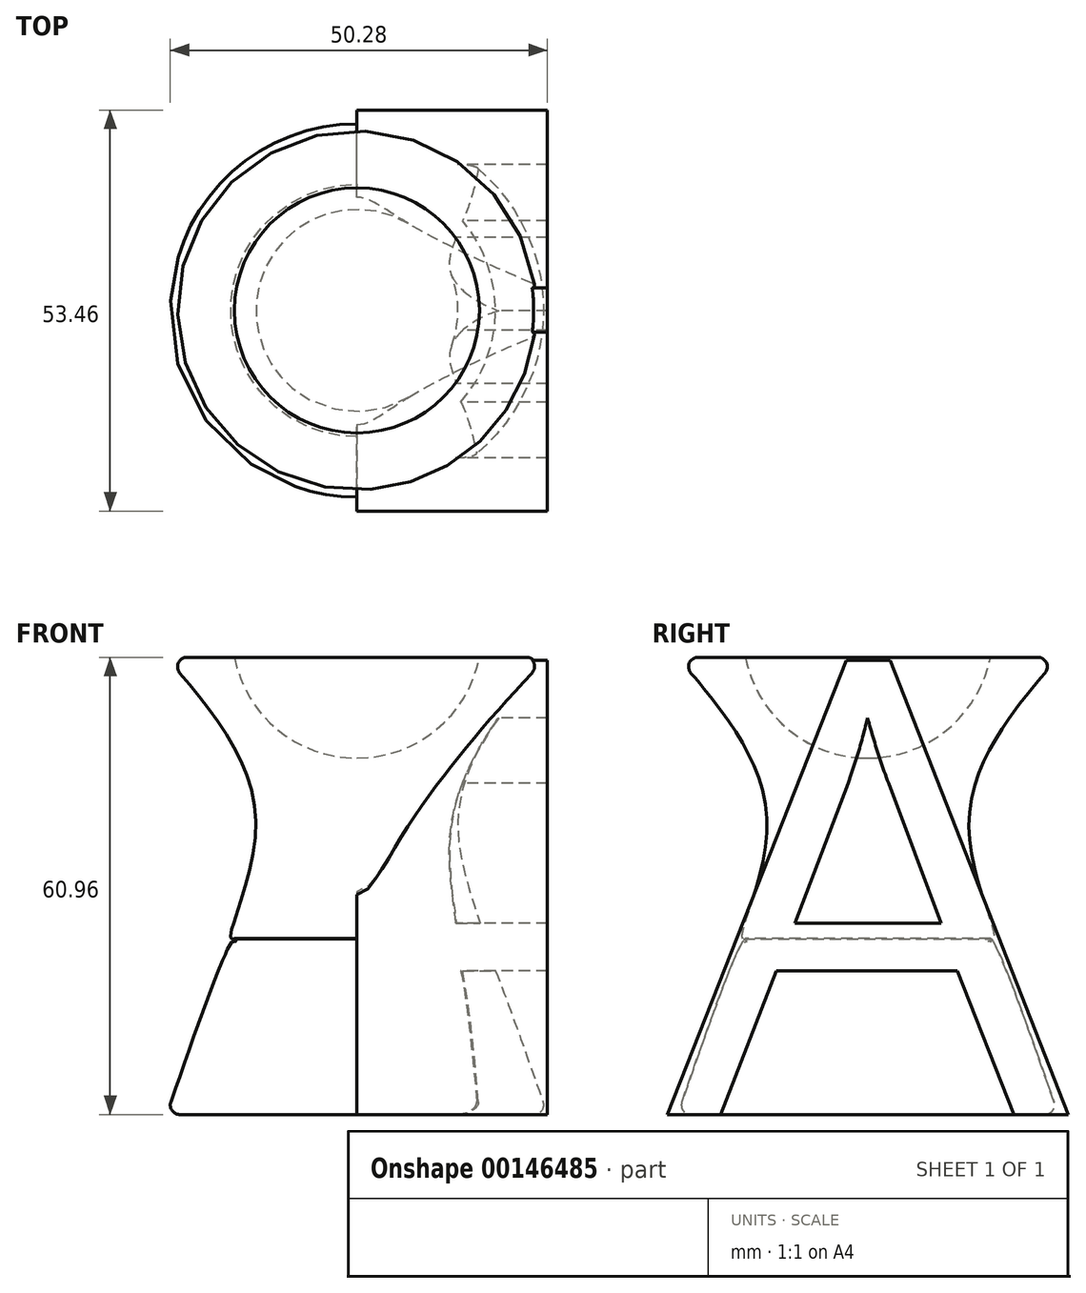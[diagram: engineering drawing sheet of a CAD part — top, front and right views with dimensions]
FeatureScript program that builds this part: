
annotation { "Feature Type Name" : "Feature", "Feature Type Description" : "" }
export const myFeature = defineFeature(function(context is Context, id is Id, definition is map)
    precondition{}
    {
        {
            var Q0;
            Q0=qCreatedBy(makeId("Top.planeOp"),FACE);
            var sketch = newSketch(context, id + "F0", { "sketchPlane" : qUnion([Q0])});
            skCircle(sketch, "E0", {"center": v(0, 0) * mm, "radius": 25.4 * mm});
            skSolve(sketch);
        }
        {
            var Q0;
            Q0=makeQuery(id+"F0.imprint","IMPRINT",FACE,{"disambiguationData":[TD([[makeQuery(id+"F0.imprint","IMPRINT",EDGE,{"derivedFrom":sQuery(id+"F0.wireOp",EDGE,"E0")}),1.0]])]});
            extrude(context, id + "F1", {"entities" : qUnion([Q0]), "depth" : 60.96 * mm});
        }
        {
            var Q0;
            Q0=qCreatedBy(makeId("Right.planeOp"),FACE);
            var sketch = newSketch(context, id + "F2", { "sketchPlane" : qUnion([Q0])});
            skLineSegment(sketch, "E1", {"start": v(-25.4, 72.87) * mm, "end": v(-25.4, 0) * mm});
            skLineSegment(sketch, "E2", {"start": v(-25.4, 0) * mm, "end": v(-25.4, -9.39) * mm});
            skLineSegment(sketch, "E3", {"start": v(0, 72.87) * mm, "end": v(0, -9.39) * mm, "construction": true});
            skLineSegment(sketch, "E4", {"start": v(-50.82, 60.96) * mm, "end": v(37.35, 60.96) * mm, "construction": true});
            skFitSpline(sketch, "E5", {"points": [v(-25.4, 60.96) * mm, v(-13.47, 38.17) * mm, v(-16.74, 23.47) * mm, v(-16.33, 23.47) * mm, v(-16.53, 23.27) * mm, v(-25.4, 0) * mm], "startDerivative": vector(54.28, -63.33) * mm, "endDerivative": vector(-34.6, -99) * mm});
            skLineSegment(sketch, "E6", {"start": v(-25.4, 60.96) * mm, "end": v(-25.4, 0) * mm});
            skSolve(sketch);
        }
        {
            var Q0;
            Q0 = qSketchRegion(id + "F2", true);
            var Q1;
            Q1=sQuery(id+"F2.wireOp",EDGE,"E3");
            revolve(context, id + "F3", {"operationType" : NewBodyOperationType.REMOVE, "entities" : qUnion([Q0]), "axis" : qUnion([Q1]), "revolveType" : RevolveType.FULL, "oppositeDirection" : true});
        }
        {
            var Q0;
            Q0=qCreatedBy(makeId("Right.planeOp"),FACE);
            var sketch = newSketch(context, id + "F4", { "sketchPlane" : qUnion([Q0])});
            skText(sketch, "E7", { "text": "A", "fontName": "OpenSans-Regular.ttf"});
            const initialGuessF4  = {"E7": [-0.02674, 0, 1, 0, 0.06082]};
            skSetInitialGuess(sketch, initialGuessF4);
            skSolve(sketch);
        }
        {
            var Q0;
            Q0 = qSketchRegion(id + "F4", true);
            var Q1;
            Q1 = qConstructionFilter(qBodyType(qCreatedBy(id + "F4" ,EDGE), BodyType.WIRE), ConstructionObject.NO);
            extrude(context, id + "F5", {"entities" : qUnion([Q0]), "operationType" : NewBodyOperationType.ADD, "surfaceEntities" : qUnion([Q1]), "depth" : 25.4 * mm});
        }
        {
            var Q0;
            Q0=qCreatedBy(makeId("Right.planeOp"),FACE);
            var sketch = newSketch(context, id + "F6", { "sketchPlane" : qUnion([Q0])});
            skArc(sketch, "E8", {"start": v(0, 47.52) * mm, "mid": v(16.65, 64.16) * mm, "end": v(0, 80.81) * mm});
            skLineSegment(sketch, "E9", {"start": v(0, 80.81) * mm, "end": v(0, 47.52) * mm});
            skSolve(sketch);
        }
        {
            var Q0;
            Q0 = qSketchRegion(id + "F6", true);
            var Q1;
            Q1=sQuery(id+"F6.wireOp",EDGE,"E9");
            revolve(context, id + "F7", {"operationType" : NewBodyOperationType.REMOVE, "entities" : qUnion([Q0]), "axis" : qUnion([Q1]), "revolveType" : RevolveType.FULL, "oppositeDirection" : true});
        }
        {
            var Q0;
            {var subQ0=sQuery(id+"F2.wireOp",EDGE,"E6");var subQ1=sQuery(id+"F2.wireOp",EDGE,"E5");Q0=makeQuery(id+"F3.boolean.opBoolean","MERGE",EDGE,{"derivedFrom":[makeQuery(id+"F1.opExtrude","CAP_EDGE",EDGE,{"disambiguationData":[OSD([sQuery(id+"F0.wireOp",EDGE,"E0")])],"isStart":false}),makeQuery(id+"F3.opRevolve","SWEPT_EDGE",EDGE,{"disambiguationData":[OSD([subQ1,subQ0]),TDD([makeQuery(id+"F2.imprint","INTERSECT",VERTEX,{"disambiguationData":[OD(0.0)],"derivedFrom":[subQ1,subQ0]})])]})]});}
            var Q1;
            {var subQ0=sQuery(id+"F4.wireOp",EDGE,"E7.sketch_text.stroke-3");var subQ1=sQuery(id+"F4.wireOp",EDGE,"E7.sketch_text.stroke-7");var subQ2=sQuery(id+"F2.wireOp",EDGE,"E5");var subQ3=sQuery(id+"F0.wireOp",EDGE,"E0");var subQ4=sQuery(id+"F2.wireOp",EDGE,"E6");Q1=makeQuery(id+"F5.boolean.opBoolean","SPLIT",EDGE,{"disambiguationData":[TD([makeQuery(id+"F5.opExtrude","CAP_FACE",FACE,{"disambiguationData":[OSD([sQuery(id+"F4.wireOp",EDGE,"E7.sketch_text.stroke-0"),sQuery(id+"F4.wireOp",EDGE,"E7.sketch_text.stroke-1"),sQuery(id+"F4.wireOp",EDGE,"E7.sketch_text.stroke-2"),subQ0,sQuery(id+"F4.wireOp",EDGE,"E7.sketch_text.stroke-4"),sQuery(id+"F4.wireOp",EDGE,"E7.sketch_text.stroke-5"),sQuery(id+"F4.wireOp",EDGE,"E7.sketch_text.stroke-6"),subQ1,sQuery(id+"F4.wireOp",EDGE,"E7.sketch_text.stroke-8"),sQuery(id+"F4.wireOp",EDGE,"E7.sketch_text.stroke-9"),sQuery(id+"F4.wireOp",EDGE,"E7.sketch_text.stroke-10"),sQuery(id+"F4.wireOp",EDGE,"E7.sketch_text.stroke-11"),sQuery(id+"F4.wireOp",EDGE,"E7.sketch_text.stroke-12")])],"isStart":true})])],"derivedFrom":makeQuery(id+"F3.boolean.opBoolean","MERGE",EDGE,{"derivedFrom":[makeQuery(id+"F1.opExtrude","CAP_EDGE",EDGE,{"disambiguationData":[OSD([subQ3])],"isStart":true}),makeQuery(id+"F3.opRevolve","SWEPT_EDGE",EDGE,{"disambiguationData":[OSD([subQ2,subQ4]),TDD([makeQuery(id+"F2.imprint","INTERSECT",VERTEX,{"disambiguationData":[OD(1.0)],"derivedFrom":[subQ2,subQ4]})])]})]})});}
            var Q2;
            {var subQ0=sQuery(id+"F2.wireOp",EDGE,"E5");var subQ1=sQuery(id+"F0.wireOp",EDGE,"E0");var subQ2=sQuery(id+"F2.wireOp",EDGE,"E6");Q2=makeQuery(id+"F5.boolean.opBoolean","SPLIT",EDGE,{"disambiguationData":[TD([makeQuery(id+"F5.opExtrude","SWEPT_FACE",FACE,{"disambiguationData":[OSD([sQuery(id+"F4.wireOp",EDGE,"E7.sketch_text.stroke-0")])]})])],"derivedFrom":makeQuery(id+"F3.boolean.opBoolean","MERGE",EDGE,{"derivedFrom":[makeQuery(id+"F1.opExtrude","CAP_EDGE",EDGE,{"disambiguationData":[OSD([subQ1])],"isStart":true}),makeQuery(id+"F3.opRevolve","SWEPT_EDGE",EDGE,{"disambiguationData":[OSD([subQ0,subQ2]),TDD([makeQuery(id+"F2.imprint","INTERSECT",VERTEX,{"disambiguationData":[OD(1.0)],"derivedFrom":[subQ0,subQ2]})])]})]})});}
            fillet(context, id + "F8", {"entities" : qUnion([Q0, Q1, Q2]), "radius" : 1.27 * mm, "tangentPropagation" : true, "allowEdgeOverflow" : false});
        }
    });
